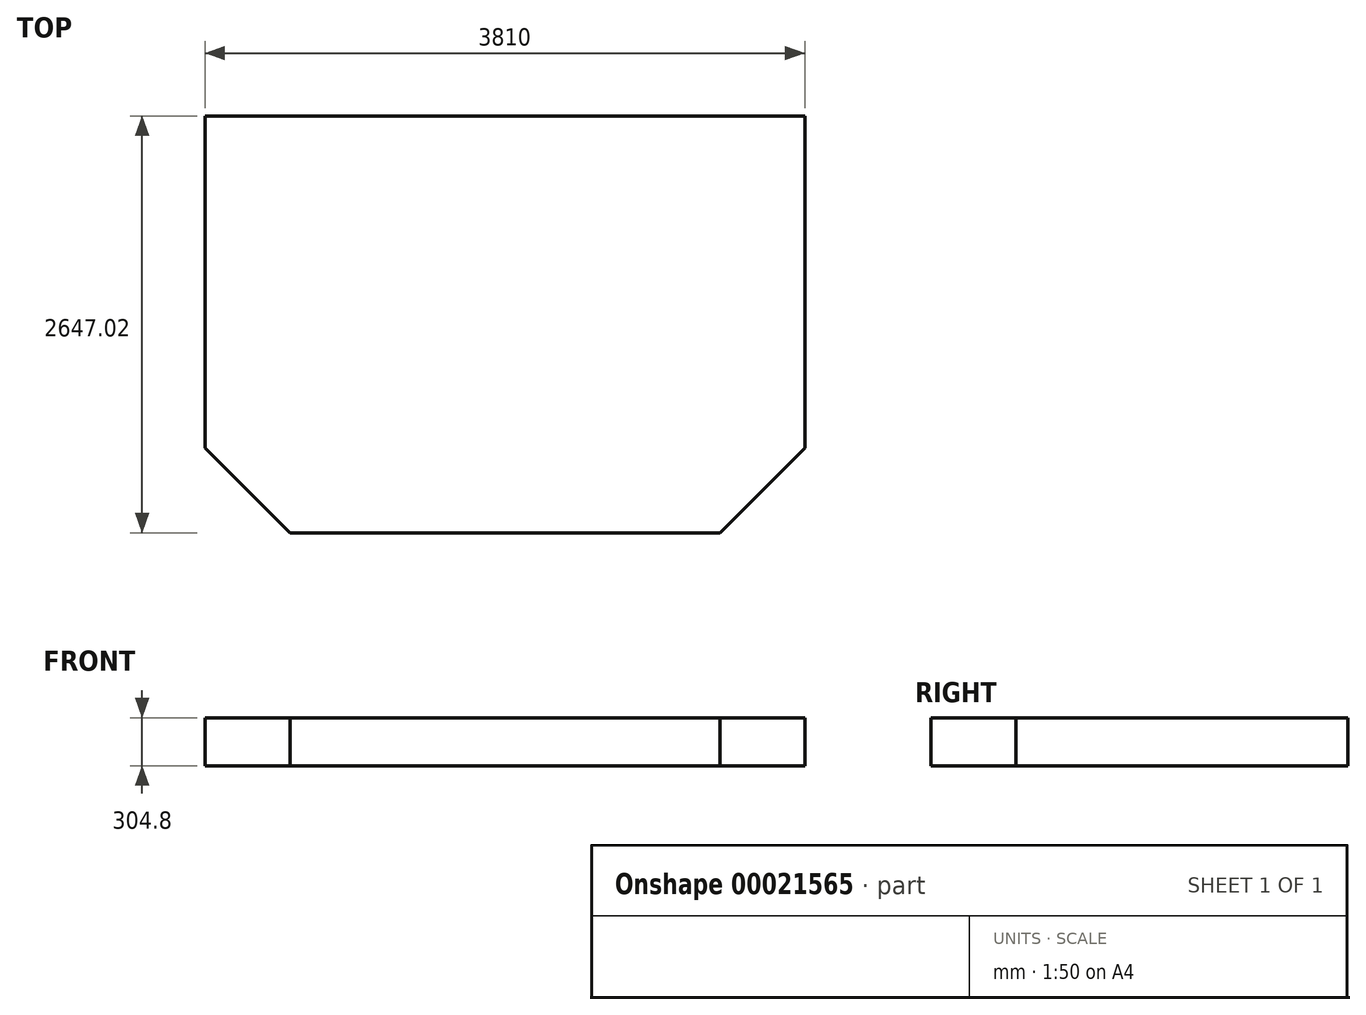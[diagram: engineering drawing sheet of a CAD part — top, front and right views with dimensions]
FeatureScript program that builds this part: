
annotation { "Feature Type Name" : "Feature", "Feature Type Description" : "" }
export const myFeature = defineFeature(function(context is Context, id is Id, definition is map)
    precondition{}
    {
        {
            var Q0;
            Q0=qCreatedBy(makeId("Top.planeOp"),FACE);
            var sketch = newSketch(context, id + "F0", { "sketchPlane" : qUnion([Q0])});
            skLineSegment(sketch, "E0", {"start": v(-6914.22, 0) * mm, "end": v(-3104.22, 0) * mm});
            skLineSegment(sketch, "E1", {"start": v(-3643.03, -2647.02) * mm, "end": v(-6375.4, -2647.02) * mm});
            skLineSegment(sketch, "E2", {"start": v(-3104.22, 0) * mm, "end": v(-3104.22, -2108.2) * mm});
            skLineSegment(sketch, "E3", {"start": v(-3104.22, -2108.2) * mm, "end": v(-3643.03, -2647.02) * mm});
            skLineSegment(sketch, "E4", {"start": v(-6914.22, 0) * mm, "end": v(-6914.22, -2108.2) * mm});
            skLineSegment(sketch, "E5", {"start": v(-6914.22, -2108.2) * mm, "end": v(-6375.4, -2647.02) * mm});
            skSolve(sketch);
        }
        {
            var Q0;
            Q0=makeQuery(id+"F0.imprint","IMPRINT",FACE,{"disambiguationData":[TD([[makeQuery(id+"F0.imprint","IMPRINT",EDGE,{"derivedFrom":sQuery(id+"F0.wireOp",EDGE,"E0")}),-1.0]])]});
            extrude(context, id + "F1", {"entities" : qUnion([Q0]), "depth" : 304.8 * mm});
        }
    });
